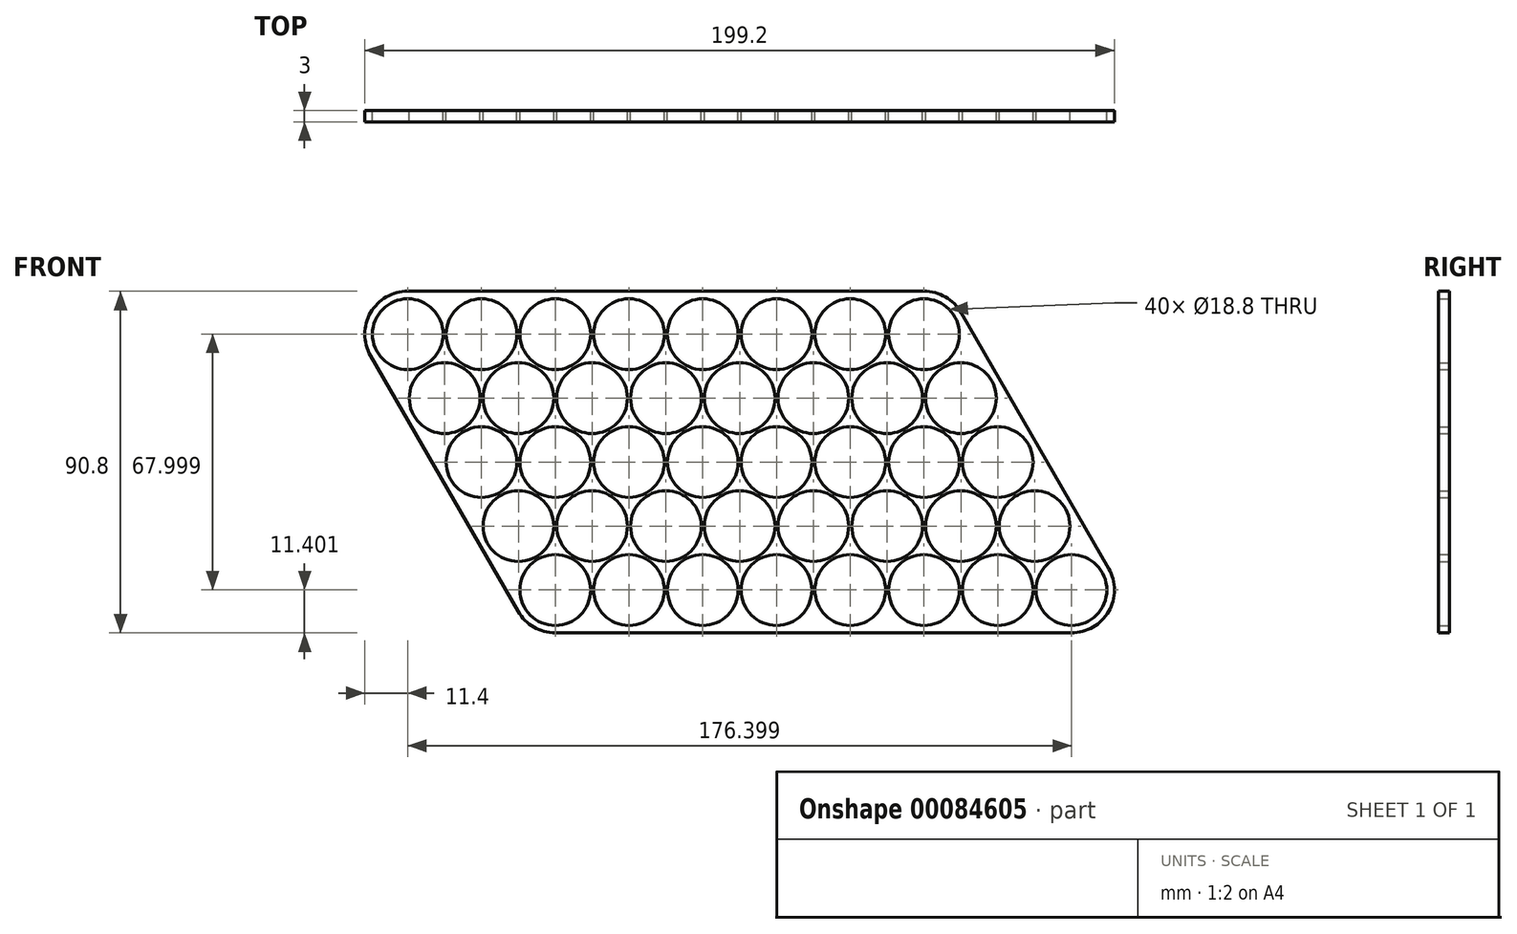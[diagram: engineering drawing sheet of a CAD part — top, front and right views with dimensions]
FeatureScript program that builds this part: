
annotation { "Feature Type Name" : "Feature", "Feature Type Description" : "" }
export const myFeature = defineFeature(function(context is Context, id is Id, definition is map)
    precondition{}
    {
        {
            var Q0;
            Q0=qCreatedBy(makeId("Front.planeOp"),FACE);
            var sketch = newSketch(context, id + "F0", { "sketchPlane" : qUnion([Q0]) });
            skCircle(sketch, "E0", {"center": v(0, 0) * mm, "radius": 9.4 * mm});
            skCircle(sketch, "E1.1.0.0", {"center": v(19.6, 0) * mm, "radius": 9.4 * mm});
            skCircle(sketch, "E1.2.0.0", {"center": v(39.2, 0) * mm, "radius": 9.4 * mm});
            skCircle(sketch, "E1.3.0.0", {"center": v(58.8, 0) * mm, "radius": 9.4 * mm});
            skLineSegment(sketch, "E1.direction1", {"start": v(0, 0) * mm, "end": v(19.6, 0) * mm, "construction": true});
            skLineSegment(sketch, "E2", {"start": v(0, -17) * mm, "end": v(73.2, -17) * mm, "construction": true});
            skLineSegment(sketch, "E3", {"start": v(9.8, 0) * mm, "end": v(9.8, -17) * mm, "construction": true});
            skCircle(sketch, "E4", {"center": v(9.8, -17) * mm, "radius": 9.4 * mm});
            skCircle(sketch, "E5.1.0.0", {"center": v(29.4, -17) * mm, "radius": 9.4 * mm});
            skCircle(sketch, "E5.2.0.0", {"center": v(49, -17) * mm, "radius": 9.4 * mm});
            skCircle(sketch, "E5.3.0.0", {"center": v(68.6, -17) * mm, "radius": 9.4 * mm});
            skLineSegment(sketch, "E5.direction1", {"start": v(9.8, -17) * mm, "end": v(29.4, -17) * mm, "construction": true});
            skLineSegment(sketch, "E6", {"start": v(-8.14, -4.7) * mm, "end": v(1.66, -21.7) * mm});
            skLineSegment(sketch, "E7", {"start": v(0, 9.4) * mm, "end": v(58.8, 9.4) * mm});
            skLineSegment(sketch, "E8", {"start": v(9.8, -17) * mm, "end": v(9.8, -26.4) * mm, "construction": true});
            skLineSegment(sketch, "E9", {"start": v(68.6, -17) * mm, "end": v(68.6, -26.4) * mm, "construction": true});
            skArc(sketch, "E10", {"start": v(58.8, 9.4) * mm, "mid": v(63.5, 8.14) * mm, "end": v(66.94, 4.7) * mm});
            skArc(sketch, "E11", {"start": v(76.74, -12.3) * mm, "mid": v(76.74, -21.7) * mm, "end": v(68.6, -26.4) * mm});
            skArc(sketch, "E12", {"start": v(9.8, -26.4) * mm, "mid": v(5.1, -25.14) * mm, "end": v(1.66, -21.7) * mm});
            skArc(sketch, "E13", {"start": v(-8.14, -4.7) * mm, "mid": v(-8.14, 4.7) * mm, "end": v(0, 9.4) * mm});
            skArc(sketch, "E14.0", {"start": v(0, 11.4) * mm, "mid": v(-9.87, 5.7) * mm, "end": v(-9.88, -5.7) * mm});
            skLineSegment(sketch, "E15.0", {"start": v(0, 11.4) * mm, "end": v(58.8, 11.4) * mm});
            skLineSegment(sketch, "E16.0", {"start": v(-9.88, -5.7) * mm, "end": v(-0.08, -22.7) * mm});
            skArc(sketch, "E17.trimOffspring", {"start": v(9.8, -5.82) * mm, "mid": v(9.87, -5.71) * mm, "end": v(9.93, -5.6) * mm});
            skArc(sketch, "E18.trimOffspring", {"start": v(9.93, -5.6) * mm, "mid": v(9.86, -5.6) * mm, "end": v(9.8, -5.6) * mm});
            skCircle(sketch, "E19.0.4.0", {"center": v(78.4, 0) * mm, "radius": 9.4 * mm});
            skCircle(sketch, "E19.0.5.0", {"center": v(98, 0) * mm, "radius": 9.4 * mm});
            skCircle(sketch, "E20.0.4.0", {"center": v(88.2, -17) * mm, "radius": 9.4 * mm});
            skCircle(sketch, "E20.0.5.0", {"center": v(107.8, -17) * mm, "radius": 9.4 * mm});
            skLineSegment(sketch, "E21", {"start": v(58.8, 11.4) * mm, "end": v(98, 11.4) * mm});
            skLineSegment(sketch, "E22", {"start": v(0, 0) * mm, "end": v(9.8, -17) * mm, "construction": true});
            skCircle(sketch, "E23.1.0.0", {"center": v(19.6, -34) * mm, "radius": 9.4 * mm});
            skCircle(sketch, "E23.2.0.0", {"center": v(29.4, -51) * mm, "radius": 9.4 * mm});
            skLineSegment(sketch, "E23.direction1", {"start": v(9.8, -17) * mm, "end": v(19.6, -34) * mm, "construction": true});
            skCircle(sketch, "E24.1.0.0", {"center": v(39.2, -34) * mm, "radius": 9.4 * mm});
            skCircle(sketch, "E24.1.0.1", {"center": v(49, -51) * mm, "radius": 9.4 * mm});
            skCircle(sketch, "E24.2.0.0", {"center": v(58.8, -34) * mm, "radius": 9.4 * mm});
            skCircle(sketch, "E24.2.0.1", {"center": v(68.6, -51) * mm, "radius": 9.4 * mm});
            skCircle(sketch, "E24.3.0.0", {"center": v(78.4, -34) * mm, "radius": 9.4 * mm});
            skCircle(sketch, "E24.3.0.1", {"center": v(88.2, -51) * mm, "radius": 9.4 * mm});
            skCircle(sketch, "E24.4.0.0", {"center": v(98, -34) * mm, "radius": 9.4 * mm});
            skCircle(sketch, "E24.4.0.1", {"center": v(107.8, -51) * mm, "radius": 9.4 * mm});
            skCircle(sketch, "E24.5.0.0", {"center": v(117.6, -34) * mm, "radius": 9.4 * mm});
            skCircle(sketch, "E24.5.0.1", {"center": v(127.4, -51) * mm, "radius": 9.4 * mm});
            skLineSegment(sketch, "E24.direction1", {"start": v(19.6, -34) * mm, "end": v(39.2, -34) * mm, "construction": true});
            skLineSegment(sketch, "E25", {"start": v(-0.08, -22.7) * mm, "end": v(19.52, -56.7) * mm});
            skArc(sketch, "E26.0", {"start": v(29.27, -62.4) * mm, "mid": v(29.33, -62.4) * mm, "end": v(29.4, -62.4) * mm});
            skCircle(sketch, "E27.0.6.0", {"center": v(117.6, 0) * mm, "radius": 9.4 * mm});
            skCircle(sketch, "E27.0.7.0", {"center": v(137.2, 0) * mm, "radius": 9.4 * mm});
            skCircle(sketch, "E28.0.6.0", {"center": v(127.4, -17) * mm, "radius": 9.4 * mm});
            skCircle(sketch, "E28.0.7.0", {"center": v(147, -17) * mm, "radius": 9.4 * mm});
            skCircle(sketch, "E29.0.6.0", {"center": v(137.2, -34) * mm, "radius": 9.4 * mm});
            skCircle(sketch, "E29.2.6.0", {"center": v(147, -51) * mm, "radius": 9.4 * mm});
            skCircle(sketch, "E29.0.7.0", {"center": v(156.8, -34) * mm, "radius": 9.4 * mm});
            skCircle(sketch, "E29.2.7.0", {"center": v(166.6, -51) * mm, "radius": 9.4 * mm});
            skArc(sketch, "E30.0", {"start": v(147.08, 5.7) * mm, "mid": v(142.9, 9.87) * mm, "end": v(137.2, 11.4) * mm});
            skLineSegment(sketch, "E31", {"start": v(98, 11.4) * mm, "end": v(137.2, 11.4) * mm});
            skLineSegment(sketch, "E32", {"start": v(147.08, 5.7) * mm, "end": v(176.48, -45.3) * mm});
            skCircle(sketch, "E33.0.3.0", {"center": v(39.2, -68) * mm, "radius": 9.4 * mm});
            skCircle(sketch, "E34.1.0.0", {"center": v(58.8, -68) * mm, "radius": 9.4 * mm});
            skCircle(sketch, "E34.2.0.0", {"center": v(78.4, -68) * mm, "radius": 9.4 * mm});
            skCircle(sketch, "E34.3.0.0", {"center": v(98, -68) * mm, "radius": 9.4 * mm});
            skCircle(sketch, "E34.4.0.0", {"center": v(117.6, -68) * mm, "radius": 9.4 * mm});
            skCircle(sketch, "E34.5.0.0", {"center": v(137.2, -68) * mm, "radius": 9.4 * mm});
            skCircle(sketch, "E34.6.0.0", {"center": v(156.8, -68) * mm, "radius": 9.4 * mm});
            skCircle(sketch, "E34.7.0.0", {"center": v(176.4, -68) * mm, "radius": 9.4 * mm});
            skLineSegment(sketch, "E34.direction1", {"start": v(39.2, -68) * mm, "end": v(58.8, -68) * mm, "construction": true});
            skArc(sketch, "E35.0", {"start": v(29.32, -73.7) * mm, "mid": v(33.5, -77.87) * mm, "end": v(39.2, -79.4) * mm});
            skArc(sketch, "E36.0", {"start": v(176.4, -79.4) * mm, "mid": v(186.27, -73.7) * mm, "end": v(186.28, -62.3) * mm});
            skLineSegment(sketch, "E37", {"start": v(19.52, -56.7) * mm, "end": v(29.32, -73.7) * mm});
            skLineSegment(sketch, "E38", {"start": v(176.48, -45.3) * mm, "end": v(186.28, -62.3) * mm});
            skLineSegment(sketch, "E39", {"start": v(39.2, -79.4) * mm, "end": v(176.4, -79.4) * mm});
            skSolve(sketch);
        }
        {
            var Q0;
            Q0=qSketchRegion(id+"F0",true);
            var Q1;
            {var subQ3=sQuery(id+"F0.wireOp",EDGE,"E1.1.0.0");Q1=makeQuery(id+"F0.imprint","IMPRINT",FACE,{"disambiguationData":[TD([[makeQuery(id+"F0.imprint","IMPRINT",EDGE,{"derivedFrom":subQ3}),-1.0]])]});}
            extrude(context, id + "F1", {"entities" : qUnion([Q0, Q1]), "depth" : 3 * mm});
        }
    });
